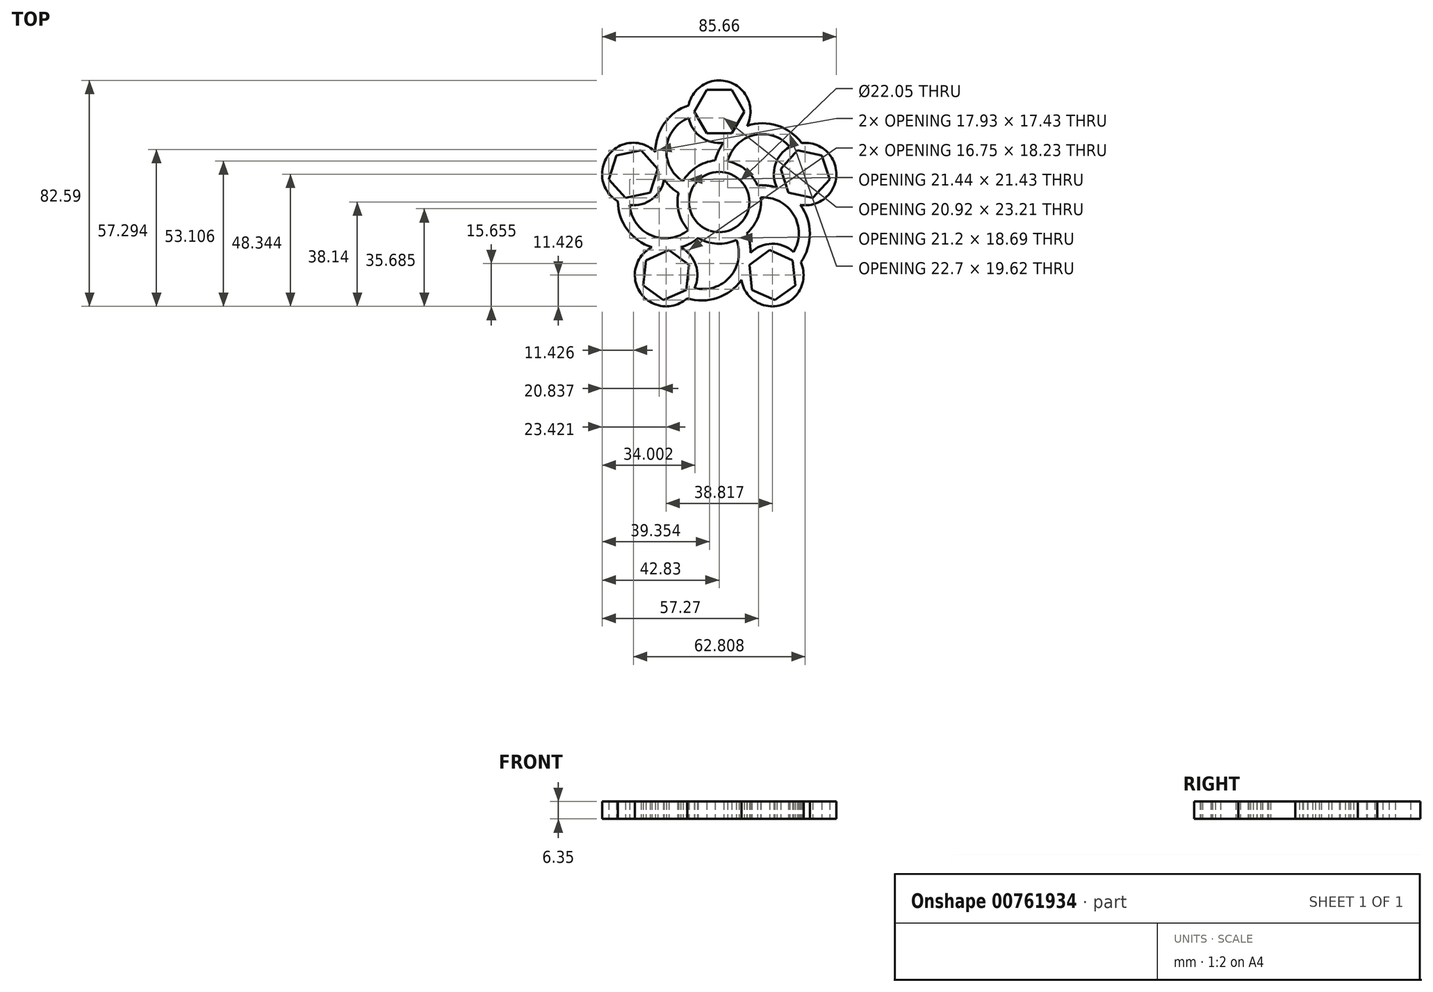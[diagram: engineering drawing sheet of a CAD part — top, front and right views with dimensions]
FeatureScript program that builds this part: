
annotation { "Feature Type Name" : "Feature", "Feature Type Description" : "" }
export const myFeature = defineFeature(function(context is Context, id is Id, definition is map)
    precondition{}
    {
        {
            var Q0;
            Q0=qCreatedBy(makeId("Top.planeOp"),FACE);
            var sketch = newSketch(context, id + "F0", { "sketchPlane" : qUnion([Q0])});
            skCircle(sketch, "E0", {"center": v(0, 0) * mm, "radius": 15.24 * mm});
            skCircle(sketch, "E1", {"center": v(0, 0) * mm, "radius": 11.02 * mm});
            skCircle(sketch, "E2", {"center": v(0, 33.02) * mm, "radius": 11.43 * mm});
            skCircle(sketch, "E3.cCircle", {"center": v(0, 33.02) * mm, "radius": 7.94 * mm, "construction": true});
            skLineSegment(sketch, "E3.0", {"start": v(4.58, 25.08) * mm, "end": v(-4.58, 25.08) * mm});
            skLineSegment(sketch, "E3.1", {"start": v(-4.58, 25.08) * mm, "end": v(-9.17, 33.02) * mm});
            skLineSegment(sketch, "E3.2", {"start": v(-9.17, 33.02) * mm, "end": v(-4.58, 40.96) * mm});
            skLineSegment(sketch, "E3.3", {"start": v(-4.58, 40.96) * mm, "end": v(4.58, 40.96) * mm});
            skLineSegment(sketch, "E3.4", {"start": v(4.58, 40.96) * mm, "end": v(9.17, 33.02) * mm});
            skLineSegment(sketch, "E3.5", {"start": v(9.17, 33.02) * mm, "end": v(4.58, 25.08) * mm});
            skPoint(sketch, "E3.0.midPoint", {"position": v(0, 25.08) * mm});
            skArc(sketch, "E4", {"start": v(-11.2, 30.76) * mm, "mid": v(-19.29, 19.77) * mm, "end": v(-13.24, 7.55) * mm});
            skArc(sketch, "E5", {"start": v(-11.2, 35.33) * mm, "mid": v(-23.22, 20.48) * mm, "end": v(-14.88, 3.29) * mm});
            skArc(sketch, "E6.1.0", {"start": v(-23.34, 18.3) * mm, "mid": v(-42.3, 6.74) * mm, "end": v(-20.14, 8.26) * mm});
            skPoint(sketch, "E6.1.1", {"position": v(-23.85, 7.75) * mm});
            skCircle(sketch, "E6.1.2", {"center": v(-31.4, 10.2) * mm, "radius": 7.94 * mm, "construction": true});
            skLineSegment(sketch, "E6.1.3", {"start": v(-37.54, 17.01) * mm, "end": v(-28.57, 18.92) * mm});
            skLineSegment(sketch, "E6.1.4", {"start": v(-22.44, 12.1) * mm, "end": v(-25.27, 3.4) * mm});
            skLineSegment(sketch, "E6.1.5", {"start": v(-25.27, 3.4) * mm, "end": v(-34.24, 1.49) * mm});
            skLineSegment(sketch, "E6.1.6", {"start": v(-40.37, 8.3) * mm, "end": v(-37.54, 17.01) * mm});
            skLineSegment(sketch, "E6.1.7", {"start": v(-28.57, 18.92) * mm, "end": v(-22.44, 12.1) * mm});
            skLineSegment(sketch, "E6.1.8", {"start": v(-34.24, 1.49) * mm, "end": v(-40.37, 8.3) * mm});
            skArc(sketch, "E6.1.9", {"start": v(-37.06, 0.27) * mm, "mid": v(-33.57, -10.15) * mm, "end": v(-24.62, -16.54) * mm});
            skArc(sketch, "E6.1.10", {"start": v(-32.71, -1.15) * mm, "mid": v(-24.77, -12.23) * mm, "end": v(-11.27, -10.26) * mm});
            skCircle(sketch, "E6.2.0", {"center": v(-19.4, -26.71) * mm, "radius": 11.43 * mm});
            skPoint(sketch, "E6.2.1", {"position": v(-14.74, -20.3) * mm});
            skCircle(sketch, "E6.2.2", {"center": v(-19.4, -26.71) * mm, "radius": 7.94 * mm, "construction": true});
            skLineSegment(sketch, "E6.2.3", {"start": v(-27.78, -30.44) * mm, "end": v(-26.82, -21.33) * mm});
            skLineSegment(sketch, "E6.2.4", {"start": v(-18.45, -17.6) * mm, "end": v(-11.04, -22.99) * mm});
            skLineSegment(sketch, "E6.2.5", {"start": v(-11.04, -22.99) * mm, "end": v(-12, -32.1) * mm});
            skLineSegment(sketch, "E6.2.6", {"start": v(-20.37, -35.83) * mm, "end": v(-27.78, -30.44) * mm});
            skLineSegment(sketch, "E6.2.7", {"start": v(-26.82, -21.33) * mm, "end": v(-18.45, -17.6) * mm});
            skLineSegment(sketch, "E6.2.8", {"start": v(-12, -32.1) * mm, "end": v(-20.37, -35.83) * mm});
            skArc(sketch, "E6.2.9", {"start": v(-11.7, -35.16) * mm, "mid": v(-0.72, -35.06) * mm, "end": v(8.12, -28.53) * mm});
            skArc(sketch, "E6.2.10", {"start": v(-9.01, -31.47) * mm, "mid": v(3.98, -27.33) * mm, "end": v(6.27, -13.9) * mm});
            skCircle(sketch, "E6.3.0", {"center": v(19.4, -26.71) * mm, "radius": 11.43 * mm});
            skPoint(sketch, "E6.3.1", {"position": v(14.74, -20.3) * mm});
            skCircle(sketch, "E6.3.2", {"center": v(19.4, -26.71) * mm, "radius": 7.94 * mm, "construction": true});
            skLineSegment(sketch, "E6.3.3", {"start": v(20.37, -35.83) * mm, "end": v(12, -32.1) * mm});
            skLineSegment(sketch, "E6.3.4", {"start": v(11.04, -22.99) * mm, "end": v(18.45, -17.6) * mm});
            skLineSegment(sketch, "E6.3.5", {"start": v(18.45, -17.6) * mm, "end": v(26.82, -21.33) * mm});
            skLineSegment(sketch, "E6.3.6", {"start": v(27.78, -30.44) * mm, "end": v(20.37, -35.83) * mm});
            skLineSegment(sketch, "E6.3.7", {"start": v(12, -32.1) * mm, "end": v(11.04, -22.99) * mm});
            skLineSegment(sketch, "E6.3.8", {"start": v(26.82, -21.33) * mm, "end": v(27.78, -30.44) * mm});
            skArc(sketch, "E6.3.9", {"start": v(29.82, -22) * mm, "mid": v(33.12, -11.52) * mm, "end": v(29.64, -1.09) * mm});
            skArc(sketch, "E6.3.10", {"start": v(27.14, -18.3) * mm, "mid": v(27.23, -4.66) * mm, "end": v(15.15, 1.67) * mm});
            skCircle(sketch, "E6.4.0", {"center": v(31.4, 10.2) * mm, "radius": 11.43 * mm});
            skPoint(sketch, "E6.4.1", {"position": v(23.85, 7.75) * mm});
            skCircle(sketch, "E6.4.2", {"center": v(31.4, 10.2) * mm, "radius": 7.94 * mm, "construction": true});
            skLineSegment(sketch, "E6.4.3", {"start": v(40.37, 8.3) * mm, "end": v(34.24, 1.49) * mm});
            skLineSegment(sketch, "E6.4.4", {"start": v(25.27, 3.4) * mm, "end": v(22.44, 12.1) * mm});
            skLineSegment(sketch, "E6.4.5", {"start": v(22.44, 12.1) * mm, "end": v(28.57, 18.92) * mm});
            skLineSegment(sketch, "E6.4.6", {"start": v(37.54, 17.01) * mm, "end": v(40.37, 8.3) * mm});
            skLineSegment(sketch, "E6.4.7", {"start": v(34.24, 1.49) * mm, "end": v(25.27, 3.4) * mm});
            skLineSegment(sketch, "E6.4.8", {"start": v(28.57, 18.92) * mm, "end": v(37.54, 17.01) * mm});
            skArc(sketch, "E6.4.9", {"start": v(30.14, 21.56) * mm, "mid": v(21.19, 27.94) * mm, "end": v(10.2, 27.85) * mm});
            skArc(sketch, "E6.4.10", {"start": v(25.79, 20.16) * mm, "mid": v(12.85, 24.45) * mm, "end": v(3.1, 14.92) * mm});
            skArc(sketch, "E7.trimOffspring", {"start": v(21.15, 5.16) * mm, "mid": v(17.6, 6) * mm, "end": v(13.97, 6.09) * mm});
            skArc(sketch, "E8.trimOffspring", {"start": v(1.63, 21.7) * mm, "mid": v(-0.26, 18.6) * mm, "end": v(-1.47, 15.17) * mm});
            skArc(sketch, "E9.trimOffspring", {"start": v(-14.08, -16.6) * mm, "mid": v(-10.72, -15.2) * mm, "end": v(-7.72, -13.14) * mm});
            skArc(sketch, "E10.trimOffspring", {"start": v(11.44, -18.52) * mm, "mid": v(11.14, -14.9) * mm, "end": v(10.1, -11.4) * mm});
            skSolve(sketch);
        }
        {
            var Q0;
            Q0=makeQuery(id+"F0.imprint","IMPRINT",FACE,{"disambiguationData":[TD([[makeQuery(id+"F0.imprint","IMPRINT",EDGE,{"derivedFrom":sQuery(id+"F0.wireOp",EDGE,"E6.1.3")}),1.0]])]});
            var Q1;
            {var subQ5=sQuery(id+"F0.wireOp",EDGE,"E4");Q1=makeQuery(id+"F0.imprint","IMPRINT",FACE,{"disambiguationData":[TD([[makeQuery(id+"F0.imprint","IMPRINT",EDGE,{"derivedFrom":subQ5}),-1.0]])]});}
            var Q2;
            {var subQ1=sQuery(id+"F0.wireOp",EDGE,"E6.1.9");Q2=makeQuery(id+"F0.imprint","IMPRINT",FACE,{"disambiguationData":[TD([[makeQuery(id+"F0.imprint","IMPRINT",EDGE,{"derivedFrom":subQ1}),1.0]])]});}
            var Q3;
            Q3=makeQuery(id+"F0.imprint","IMPRINT",FACE,{"disambiguationData":[TD([[makeQuery(id+"F0.imprint","IMPRINT",EDGE,{"derivedFrom":sQuery(id+"F0.wireOp",EDGE,"E6.2.3")}),1.0]])]});
            var Q4;
            {var subQ1=sQuery(id+"F0.wireOp",EDGE,"E6.2.9");Q4=makeQuery(id+"F0.imprint","IMPRINT",FACE,{"disambiguationData":[TD([[makeQuery(id+"F0.imprint","IMPRINT",EDGE,{"derivedFrom":subQ1}),1.0]])]});}
            var Q5;
            Q5=makeQuery(id+"F0.imprint","IMPRINT",FACE,{"disambiguationData":[TD([[makeQuery(id+"F0.imprint","IMPRINT",EDGE,{"derivedFrom":sQuery(id+"F0.wireOp",EDGE,"E6.3.3")}),1.0]])]});
            var Q6;
            {var subQ1=sQuery(id+"F0.wireOp",EDGE,"E6.3.9");Q6=makeQuery(id+"F0.imprint","IMPRINT",FACE,{"disambiguationData":[TD([[makeQuery(id+"F0.imprint","IMPRINT",EDGE,{"derivedFrom":subQ1}),1.0]])]});}
            var Q7;
            Q7=makeQuery(id+"F0.imprint","IMPRINT",FACE,{"disambiguationData":[TD([[makeQuery(id+"F0.imprint","IMPRINT",EDGE,{"derivedFrom":sQuery(id+"F0.wireOp",EDGE,"E6.4.3")}),1.0]])]});
            var Q8;
            {var subQ0=sQuery(id+"F0.wireOp",EDGE,"E6.4.9");Q8=makeQuery(id+"F0.imprint","IMPRINT",FACE,{"disambiguationData":[TD([[makeQuery(id+"F0.imprint","IMPRINT",EDGE,{"derivedFrom":subQ0}),1.0]])]});}
            var Q9;
            Q9=makeQuery(id+"F0.imprint","IMPRINT",FACE,{"disambiguationData":[TD([[makeQuery(id+"F0.imprint","IMPRINT",EDGE,{"derivedFrom":sQuery(id+"F0.wireOp",EDGE,"E3.0")}),1.0]])]});
            var Q10;
            Q10=makeQuery(id+"F0.imprint","IMPRINT",FACE,{"disambiguationData":[TD([[makeQuery(id+"F0.imprint","IMPRINT",EDGE,{"derivedFrom":sQuery(id+"F0.wireOp",EDGE,"E1")}),-1.0]])]});
            extrude(context, id + "F1", {"entities" : qUnion([Q0, Q1, Q2, Q3, Q4, Q5, Q6, Q7, Q8, Q9, Q10]), "depth" : 6.35 * mm, "offsetDistance" : 25.4 * mm});
        }
    });
